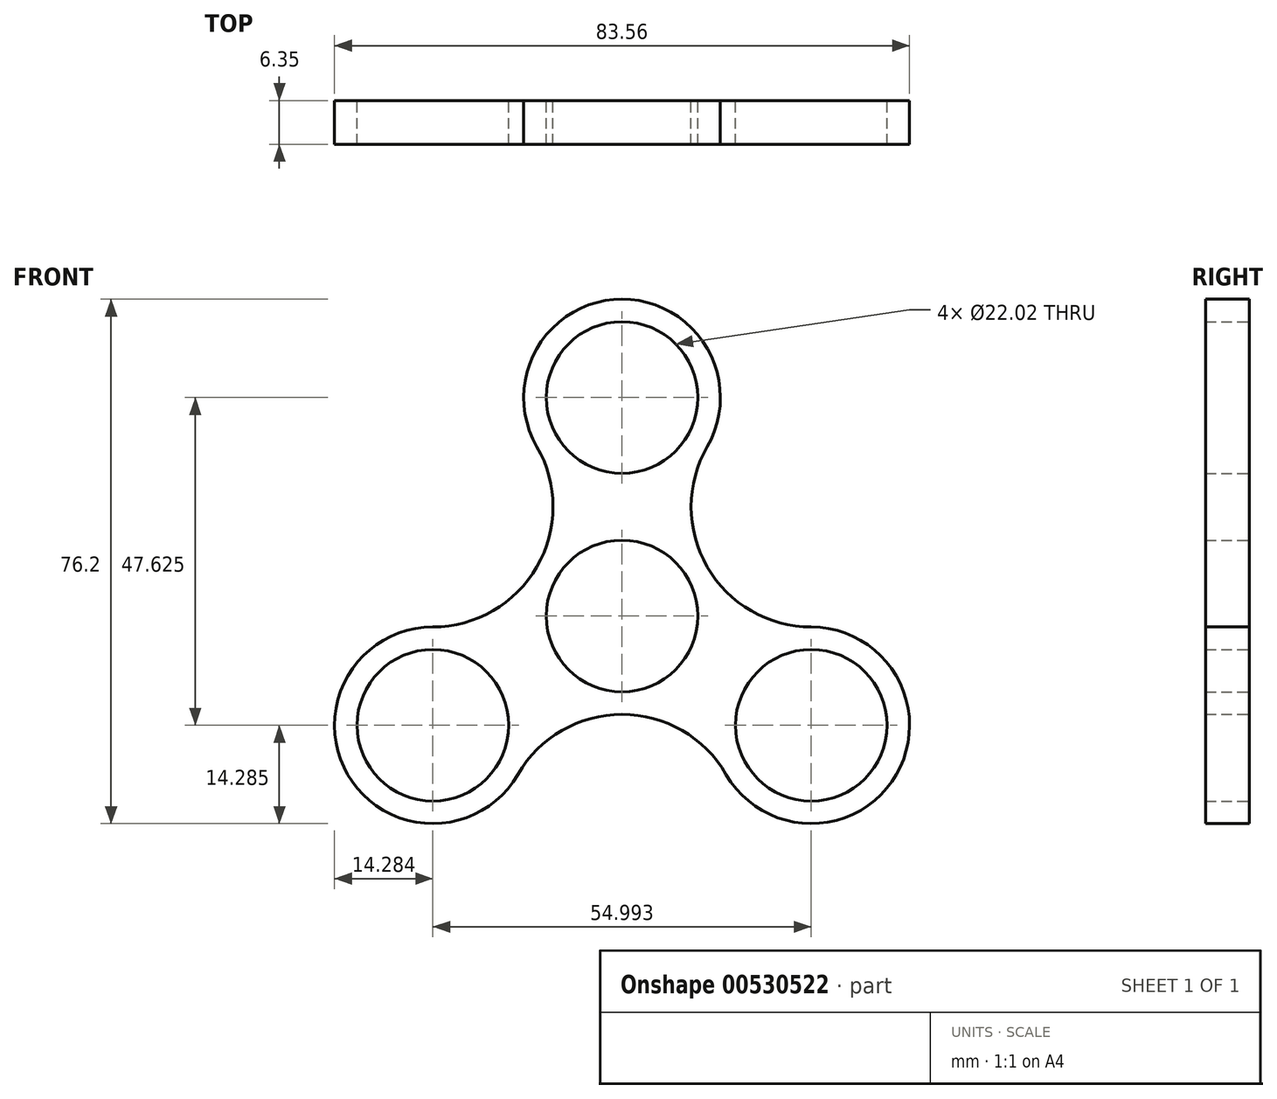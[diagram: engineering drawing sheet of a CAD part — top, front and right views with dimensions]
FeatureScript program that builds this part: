
annotation { "Feature Type Name" : "Feature", "Feature Type Description" : "" }
export const myFeature = defineFeature(function(context is Context, id is Id, definition is map)
    precondition{}
    {
        {
            var Q0;
            Q0=qCreatedBy(makeId("Front.planeOp"),FACE);
            var sketch = newSketch(context, id + "F0", { "sketchPlane" : qUnion([Q0])});
            skCircle(sketch, "E0", {"center": v(0, 0) * mm, "radius": 11.01 * mm});
            skCircle(sketch, "E1", {"center": v(0, 0) * mm, "radius": 14.29 * mm});
            skCircle(sketch, "E2", {"center": v(0, 31.75) * mm, "radius": 11.01 * mm});
            skCircle(sketch, "E3", {"center": v(0, 31.75) * mm, "radius": 14.29 * mm});
            skCircle(sketch, "E4.1.0", {"center": v(-27.5, -15.87) * mm, "radius": 11.01 * mm});
            skCircle(sketch, "E4.1.1", {"center": v(-27.5, -15.87) * mm, "radius": 14.29 * mm});
            skCircle(sketch, "E4.2.0", {"center": v(27.5, -15.88) * mm, "radius": 11.01 * mm});
            skCircle(sketch, "E4.2.1", {"center": v(27.5, -15.88) * mm, "radius": 14.29 * mm});
            skArc(sketch, "E5", {"start": v(-27.5, -1.59) * mm, "mid": v(-12.37, 7.14) * mm, "end": v(-12.37, 24.6) * mm});
            skArc(sketch, "E6", {"start": v(12.37, 24.6) * mm, "mid": v(12.37, 7.14) * mm, "end": v(27.5, -1.59) * mm});
            skArc(sketch, "E7", {"start": v(15.12, -23.02) * mm, "mid": v(0, -14.29) * mm, "end": v(-15.12, -23.02) * mm});
            skSolve(sketch);
        }
        {
            var Q0;
            Q0=makeQuery(id+"F0.imprint","IMPRINT",FACE,{"disambiguationData":[TD([[makeQuery(id+"F0.imprint","IMPRINT",EDGE,{"derivedFrom":sQuery(id+"F0.wireOp",EDGE,"E2")}),-1.0]])]});
            var Q1;
            {var subQ0=sQuery(id+"F0.wireOp",EDGE,"E5");var subQ1=sQuery(id+"F0.wireOp",EDGE,"E1");var subQ2=makeQuery(id+"F0.imprint","INTERSECT",VERTEX,{"derivedFrom":[subQ1,subQ0]});Q1=makeQuery(id+"F0.imprint","IMPRINT",FACE,{"disambiguationData":[TD([[makeQuery(id+"F0.imprint","IMPRINT",EDGE,{"disambiguationData":[TD([[subQ2,1.0]])],"derivedFrom":subQ1}),-1.0]])]});}
            var Q2;
            {var subQ0=sQuery(id+"F0.wireOp",EDGE,"E5");var subQ1=sQuery(id+"F0.wireOp",EDGE,"E1");var subQ2=makeQuery(id+"F0.imprint","INTERSECT",VERTEX,{"derivedFrom":[subQ1,subQ0]});Q2=makeQuery(id+"F0.imprint","IMPRINT",FACE,{"disambiguationData":[TD([[makeQuery(id+"F0.imprint","IMPRINT",EDGE,{"disambiguationData":[TD([[subQ2,-1.0]])],"derivedFrom":subQ1}),-1.0]])]});}
            var Q3;
            Q3=makeQuery(id+"F0.imprint","IMPRINT",FACE,{"disambiguationData":[TD([[makeQuery(id+"F0.imprint","IMPRINT",EDGE,{"derivedFrom":sQuery(id+"F0.wireOp",EDGE,"E0")}),-1.0]])]});
            var Q4;
            {var subQ0=sQuery(id+"F0.wireOp",EDGE,"E6");var subQ1=sQuery(id+"F0.wireOp",EDGE,"E1");var subQ2=makeQuery(id+"F0.imprint","INTERSECT",VERTEX,{"derivedFrom":[subQ1,subQ0]});Q4=makeQuery(id+"F0.imprint","IMPRINT",FACE,{"disambiguationData":[TD([[makeQuery(id+"F0.imprint","IMPRINT",EDGE,{"disambiguationData":[TD([[subQ2,1.0]])],"derivedFrom":subQ1}),-1.0]])]});}
            var Q5;
            Q5=makeQuery(id+"F0.imprint","IMPRINT",FACE,{"disambiguationData":[TD([[makeQuery(id+"F0.imprint","IMPRINT",EDGE,{"derivedFrom":sQuery(id+"F0.wireOp",EDGE,"E4.2.0")}),-1.0]])]});
            var Q6;
            Q6=makeQuery(id+"F0.imprint","IMPRINT",FACE,{"disambiguationData":[TD([[makeQuery(id+"F0.imprint","IMPRINT",EDGE,{"derivedFrom":sQuery(id+"F0.wireOp",EDGE,"E4.1.0")}),-1.0]])]});
            extrude(context, id + "F1", {"entities" : qUnion([Q0, Q1, Q2, Q3, Q4, Q5, Q6]), "depth" : 6.35 * mm, "offsetDistance" : 25.4 * mm});
        }
    });
